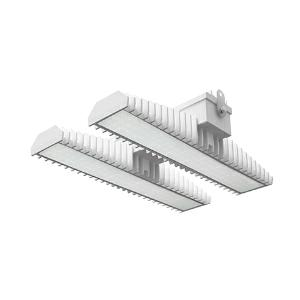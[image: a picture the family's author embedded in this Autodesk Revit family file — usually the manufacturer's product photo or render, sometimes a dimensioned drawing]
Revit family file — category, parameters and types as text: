
# Revit family: 3f_filippi_-_3f_lem_ampio_3f_filippi_-_58882_a0812_-_3f_lem_2_led_100_cr_ampio___vs_6583
name_source: partatom
category: Lighting Fixtures
units: mm (PartAtom-declared; Revit-internal decimal feet)

## family parameters
Cut with Voids When Loaded = No
Host = Face
Light Source = No
Part Type = Normal
Room Calculation Point = No
Round Connector Dimension = Use Diameter
Shared = No

## types (1)
- 3F Filippi - 3F LEM Ampio (1 x LED, 13304 lm, 109 W, 4000 K)
    Apparent Load = 109 VA
    Approval mark = CE
    CIE Flux Codes = 67 90 97 100 100
    Color Rendering = 80
    Color Temperature = 4000 K
    Control Gear = Electronic ballast
    Default Elevation = 1800 mm
    Description = Industrial luminaire with high light output and high luminous efficiency designed with the most innovative technologies for environments with temperature up to 55°C.

ILLUMINOTECHNICAL
Luminous efficiency 100% (DLOR 98%, ULOR 2%).
Initial luminous flux of the luminaire 13304 lm.
Direct symmetric wide distribution: the illuminated area has a rectangular shape.
Installation Interdistance Transv.D = 1.24 x hu - Long.D = 1.20 x hu.
Tabular UGR (CIE 117 - 4H-8H; S=0.25H; 70/50/20): RUG 22.1 - 22.2.
Beam angle: 82° - 83°.
Luminous efficacy 122 lm/W.
Lifetime (L93/B10): 30000 h. (tq+25°C)
Lifetime (L90/B10): 50000 h. (tq+25°C)
Lifetime (L85/B10): 80000 h. (tq+25°C)
Lifetime (L80/B10): 100000 h. (tq+25°C)
Lifetime (L85/B10): 50000 h. (tq+55°C)
Sudden decreased luminous flux after 50000 hours: 0% (C0).
Photobiological safety in compliance with IEC/TR 62778: RG0 risk exempt, (IEC 62471).
In compliance with IEC/EN 62722-2-1 - IEC/EN 62717 standards.

SOURCE
2 Mid-Power linear LED modules 50W/840.
Energy efficiency class (UE 2019/2020 - UE 2019/2015): C.
CIE 13.3 Colour rendering index: CRI >80 (R9 <50%).
IES TM-30 Fidelity Index: Rf = 84 Rg = 95.
CCT nominal colour temperature 4000 K.
Colour initial tolerance (MacAdam): SDCM 3.

MECHANICAL
Passive modular heatsinks in die-casted aluminium, painted in white colour.
To optimize the thermal management of the LED module, the heatsinks are oversized and provided with self-cleaning of cooling fins.
Wiring body in aluminium and galvanised steel anchored solidly to the sinks and thermally separated.
3F Lens lenses with high luminous efficiency, transparent methacrylate (PMMA), fixed to the LED modules.
Fixing brackets in stainless steel.
Luminaire with limited surface temperature. - D - (EN 60598-2-24)
Dimensions: 470x542 mm, height 133 mm. Weight 10.095 kg.
IP65 protection degree.
Mechanical strength to impacts IK06 (1 joule).
Glow-wire test resistance 650°C.

ELECTRICAL
Halogen Free electronic wiring 230V-50/60Hz, power factor 0.97, THD <25%, constant output current, class I, 1 driver.
Power of the luminaire 109 W.
ENEC - CE.
SAFE FLICKER: PstLM=<1 and SVM=<0.4 (IEC TR 61547-1 and IEC TR 63158), to ensure a more comfortable and safe light.
Luminaire compliant with EN 60598-2-22 for power supply from a centralised emergency system CPSS (Central Power Supply System), not incorporated in the luminaire - high risk areas excluded. The default power and flux are 100% in AC and 100% in DC.
Ambient temperature from -30°C to +55°C.
Temperature class T6 max 85°C.
Quick connection via M20 3P connector with 9-13 mm tightening range.
Power unit positioned on a separate compartment by the LED module to ensure optimum temperatures of cabling components, to be inspectable and maintainable.
Relative humidity UR: <85%.

INSTALLATION
Ceiling / Suspended / Wall.
All accessories dedicated to this product are available on the Catalog and on our website www.3F-Filippi.com.

ACCESSORIES
A0812 - Anti-glare microprismatic VS moulded glass, tempered, not flammable, with sealing gasket.
One required for each light module. The pack contains 10 pieces.

APPLICATIONS
In commercial environments, exhibition and industrial areas, stores, open areas.
Applications with high ambient temperature up to 55°C.
Environments in which it is necessary a total protection against falling fragments (eg environments with foodstuffs or machines with moving parts or with extreme temperature changes), use luminaires with polycarbonate lenses.

WARNING
Fixture not suitable for cold stores with an ambient temperature <0°C and/or relative humidity >85%.
Luminaire designed for disposal/recycling at end-of-life.
Replaceable (LED only) light source by a professional. Replaceable control gear by a professional.
    Height = 133 mm  [stored 0.436352 ft]
    Lamp = 1 x LED
    Lamp Light Flux = 13304 lm
    Lamp Power = 109 W
    Lamp count = 1
    Length = 470 mm
    Lifetime = 50000 h
    Luminous efficacy = 122 lm/W
    Manufacturer = 3F Filippi
    ModVariant = No
    Model = 3F Filippi - 58882+A0812 - 3F LEM 2 LED 100 CR AMPIO + VS
    Mounting Place = Ceiling
    Mounting Type = Pendant
    Number of Poles = 1
    OnlyDefault = Yes
    Power Factor = 1
    Product Name = 3F Filippi - 3F LEM Ampio
    Product group = pendant luminaire
    ProductGroupID = 9
    Protection Class = Protection class I
    Protection Degree = IP 65
    RLX_Detail_Level = 1
    RLX_Emergency_Light_Flux = 0 lm
    RLX_Emergency_Type = 0
    RLX_Emergency_Type_DB = No
    RlxData = <blob elided: 95269 chars, md5=b5b9e7f1>
    Socket = socket
    Standby Power = 0 W
    System Light Flux = 13304 lm
    System Power = 109 W
    Type Comments = Product without accessories
    Type Image = 3f_filippi_-_lem_2__a0812.jpg
    URL = http://relux.com
    VarID = ---
    Voltage = 0 V
    Weight = 0.00 kg
    Width = 542 mm

note: [stored X ft] marks values corroborated as IEEE doubles in the binary element streams (Revit-internal decimal feet)

## geometry (parser evidence)
native form markers: Blend x4, Sweep x13
no freeform markers — native parametric forms only
